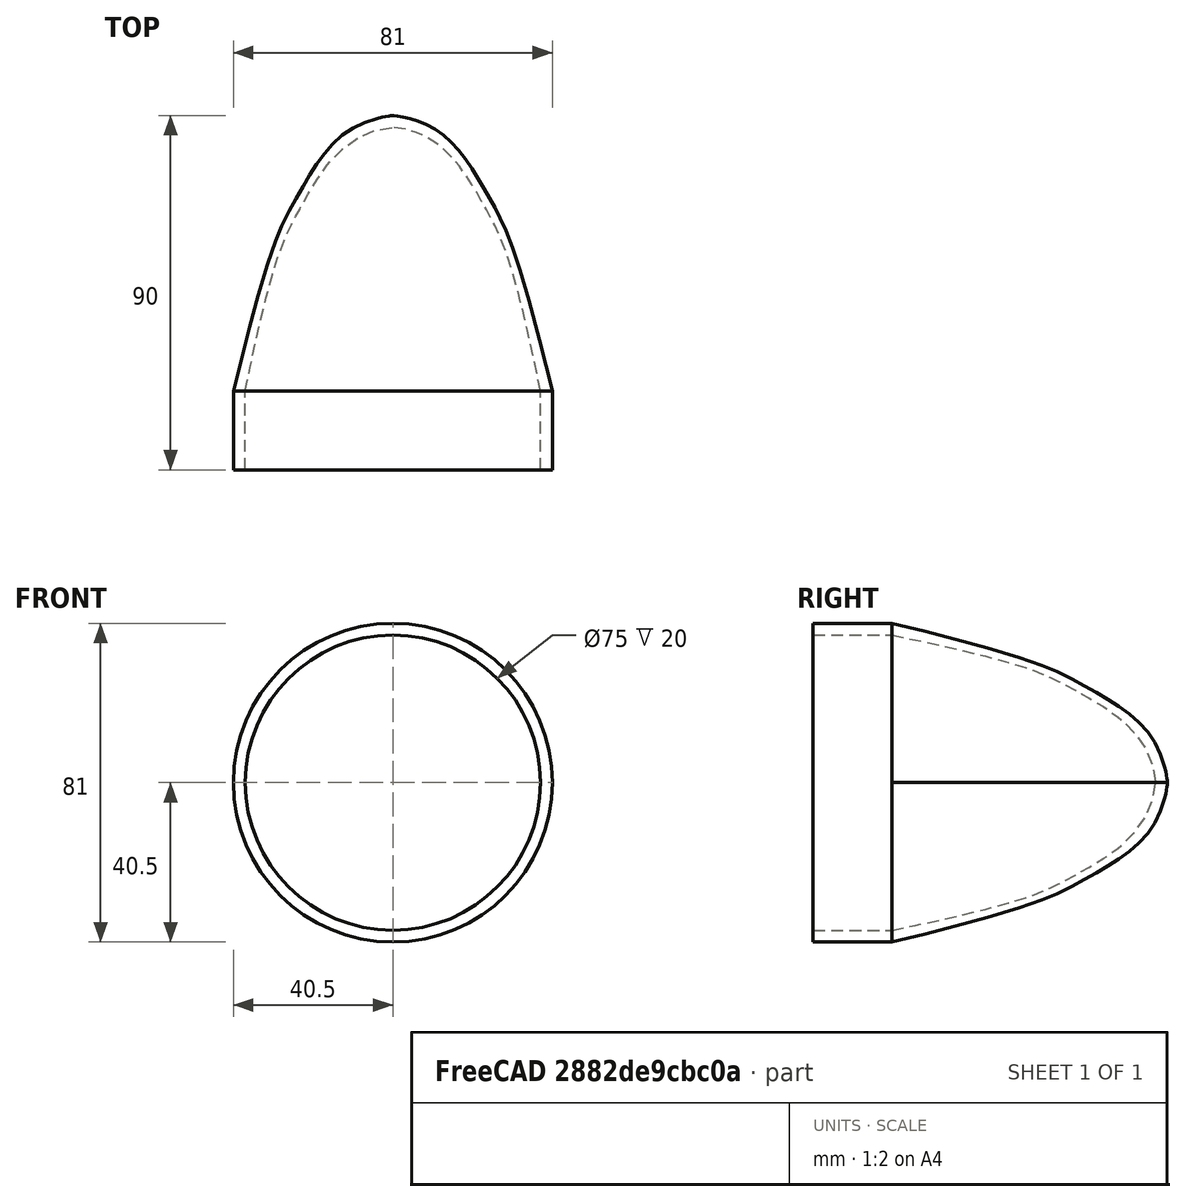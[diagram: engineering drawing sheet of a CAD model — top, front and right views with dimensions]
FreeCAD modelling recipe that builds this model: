
FCSTD DOCUMENT  (FreeCAD 0.18R16131 (Git))
Label: S200_Head_v1
License: All rights reserved
LicenseURL: http://en.wikipedia.org/wiki/All_rights_reserved
objects: Sketcher::SketchObject×1, PartDesign::Revolution×1, PartDesign::Body×1
note: 4 computed .brp shape members not serialized (recipe doc carries the construction recipe); baked Part::Feature solids carry a one-line shape summary decoded from their .brp

FEATURE [Sketcher::SketchObject] Sketch
  MapMode = 5
  Support = -> [XY_Plane]
  sketch-geometry (24):
    g0: LineSegment StartX=37.5 StartY=40 StartZ=0 EndX=37.5 EndY=60 EndZ=0
    g1: LineSegment StartX=40.5 StartY=40 StartZ=0 EndX=40.5 EndY=60 EndZ=0
    g2-g7: Circle [constr] x6 (B-spline internal-alignment scaffolding for g8; pole/knot coordinates omitted)
    g8: BSplineCurve PolesCount=6 KnotsCount=4 Degree=3 IsPeriodic=0
    g9-g12: GeomPoint [constr] x4 (B-spline internal-alignment scaffolding for g8; pole/knot coordinates omitted)
    g13-g17: Circle [constr] x5 (B-spline internal-alignment scaffolding for g18; pole/knot coordinates omitted)
    g18: BSplineCurve PolesCount=5 KnotsCount=3 Degree=3 IsPeriodic=0
    g19: GeomPoint [constr] X=37.5 Y=60 Z=0
    g20: GeomPoint [constr] X=23.1559 Y=107.122 Z=0
    g21: GeomPoint [constr] X=0 Y=127 Z=0
    g22: LineSegment StartX=0 StartY=130 StartZ=0 EndX=0 EndY=127 EndZ=0
    g23: LineSegment StartX=37.5 StartY=40 StartZ=0 EndX=40.5 EndY=40 EndZ=0
  constraints (38):
    c: Vertical(g0)
    c: Vertical(g1)
    c: DistanceX(g0,g1) = 3
    c: Coincident(g8,g1)
    c: Radius(g2) = 3
    c: Equal(g2, g3-g6) x4
    c: PointOnObject(g6,g-2)
    c: Equal(g2,g7)
    c: Coincident(g8,g6)
    c: InternalAlignment(g2-g7 -> g8) x6
    c: InternalAlignment(g9-g12 -> g8) x4
    c: DistanceY(g1,g8) = 70
    c: DistanceY(g1,g3) = 37
    c: DistanceX(g3,g1) = 9
    c: DistanceY(g3,g4) = 10
    c: DistanceX(g4,g3) = 6
    c: DistanceY(g4,g5) = 22
    c: DistanceX(g5,g4) = 12
    c: Coincident(g18,g0)
    c: Radius(g13) = 6
    c: Equal(g13, g14-g17) x4
    c: PointOnObject(g18,g-2)
    c: InternalAlignment(g13-g17 -> g18) x5
    c: InternalAlignment(g19,g18)
    c: InternalAlignment(g20,g18)
    c: Distance(g14,g3) = 3
    c: Distance(g16,g5) = 3
    c: Distance(g18,g8) = 3
    c: Distance(g4,g15) = 3
    c: Coincident(g22,g8)
    c: Coincident(g22,g18)
    c: DistanceX(g-1,g1) = 40.5
    c: DistanceY(g0,g0) = 20
    c: Equal(g0,g1)
    c: DistanceY(g-1,g1) = 40
    c: Coincident(g23,g0)
    c: Coincident(g23,g1)
    c: Horizontal(g23)
FEATURE [PartDesign::Revolution] Revolution
  Angle = 360
  Axis = (1e-16,1,-1e-16)
  Base = (0,0,0)
  Profile = -> Sketch
  ReferenceAxis = -> Y_Axis
  Reversed = true
FEATURE [PartDesign::Body] Body
  Group = -> [Sketch,Revolution]
  Origin = -> Origin
  Tip = -> Revolution
